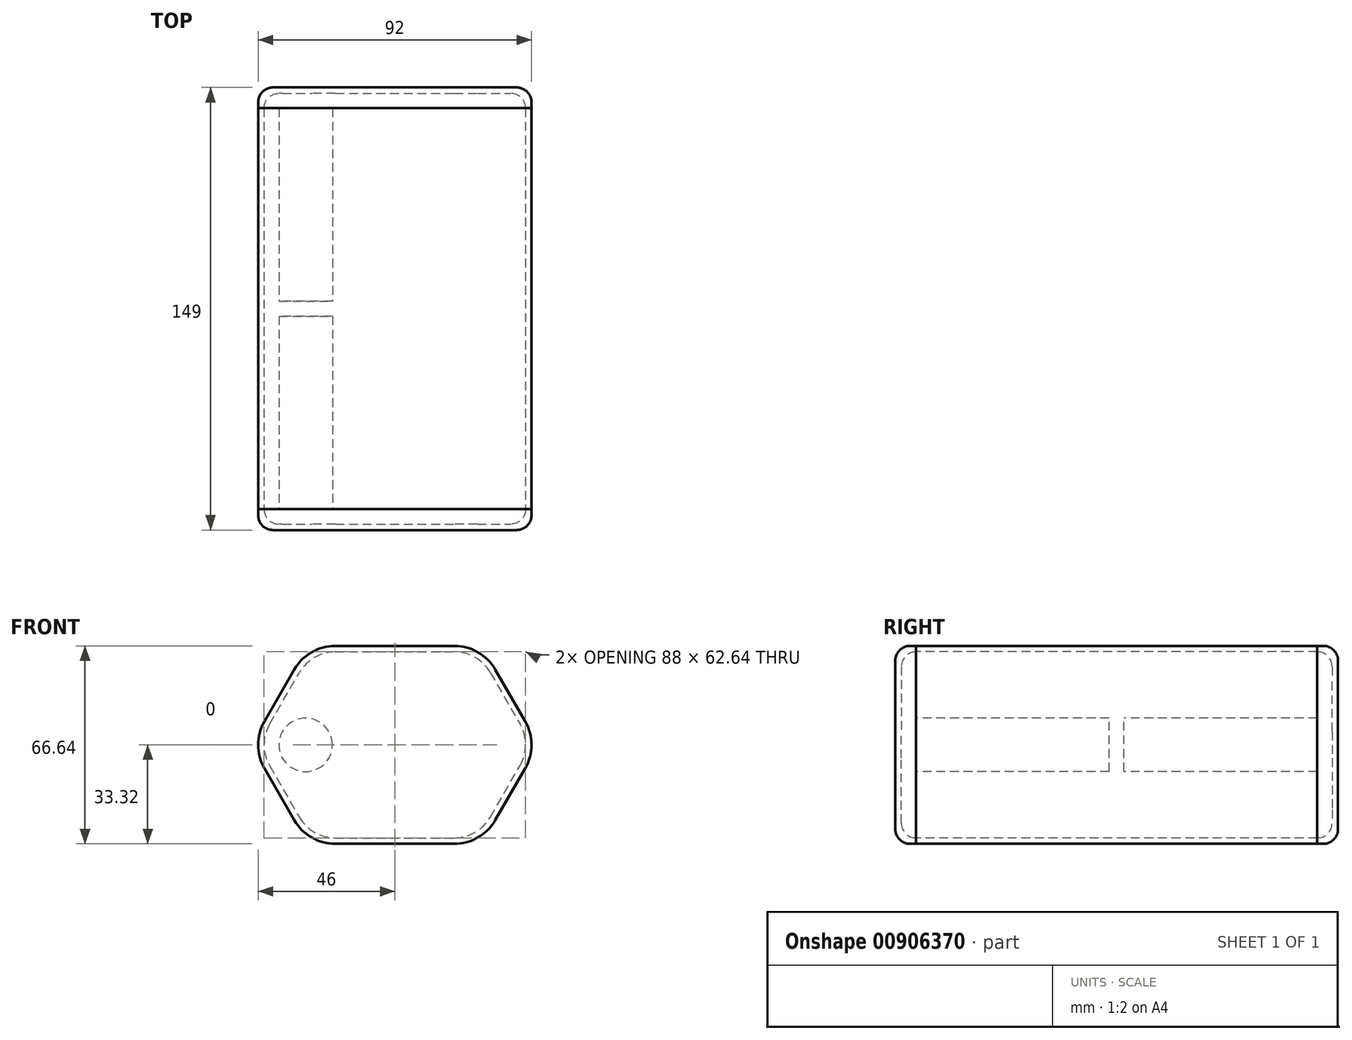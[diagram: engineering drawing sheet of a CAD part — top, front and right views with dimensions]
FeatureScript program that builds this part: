
annotation { "Feature Type Name" : "Feature", "Feature Type Description" : "" }
export const myFeature = defineFeature(function(context is Context, id is Id, definition is map)
    precondition{}
    {
        {
            var Q0;
            Q0=qCreatedBy(makeId("Front.planeOp"),FACE);
            var sketch = newSketch(context, id + "F0", { "sketchPlane" : qUnion([Q0])});
            skCircle(sketch, "E0", {"center": v(0, 0) * mm, "radius": 9 * mm});
            skCircle(sketch, "E1", {"center": v(10, 17.32) * mm, "radius": 9 * mm});
            skCircle(sketch, "E2.1.0.0", {"center": v(20, 0) * mm, "radius": 9 * mm});
            skCircle(sketch, "E2.2.0.0", {"center": v(40, 0) * mm, "radius": 9 * mm});
            skCircle(sketch, "E2.3.0.0", {"center": v(60, 0) * mm, "radius": 9 * mm});
            skLineSegment(sketch, "E2.direction1", {"start": v(0, 0) * mm, "end": v(20, 0) * mm, "construction": true});
            skCircle(sketch, "E3.1.0.0", {"center": v(30, 17.32) * mm, "radius": 9 * mm});
            skCircle(sketch, "E3.2.0.0", {"center": v(50, 17.32) * mm, "radius": 9 * mm});
            skLineSegment(sketch, "E3.direction1", {"start": v(10, 17.32) * mm, "end": v(30, 17.32) * mm, "construction": true});
            skCircle(sketch, "E4", {"center": v(10, -17.32) * mm, "radius": 9 * mm});
            skCircle(sketch, "E5.1.0.0", {"center": v(30, -17.32) * mm, "radius": 9 * mm});
            skCircle(sketch, "E5.2.0.0", {"center": v(50, -17.32) * mm, "radius": 9 * mm});
            skLineSegment(sketch, "E5.direction1", {"start": v(10, -17.32) * mm, "end": v(30, -17.32) * mm, "construction": true});
            skSolve(sketch);
        }
        {
            var Q0;
            Q0=qCreatedBy(makeId("Front.planeOp"),FACE);
            var sketch = newSketch(context, id + "F1", { "sketchPlane" : qUnion([Q0])});
            skArc(sketch, "E6.0", {"start": v(10, 26.32) * mm, "mid": v(5.5, 25.11) * mm, "end": v(2.2, 21.82) * mm});
            skArc(sketch, "E7.0", {"start": v(-7.8, 4.5) * mm, "mid": v(-9, 0) * mm, "end": v(-7.8, -4.5) * mm});
            skArc(sketch, "E8.0", {"start": v(2.2, -21.82) * mm, "mid": v(5.5, -25.11) * mm, "end": v(10, -26.32) * mm});
            skArc(sketch, "E9.0", {"start": v(57.8, 21.82) * mm, "mid": v(54.5, 25.11) * mm, "end": v(50, 26.32) * mm});
            skArc(sketch, "E10.0", {"start": v(67.8, -4.5) * mm, "mid": v(69, 0) * mm, "end": v(67.8, 4.5) * mm});
            skArc(sketch, "E11.0", {"start": v(50, -26.32) * mm, "mid": v(54.5, -25.11) * mm, "end": v(57.8, -21.82) * mm});
            skLineSegment(sketch, "E12", {"start": v(10, 26.32) * mm, "end": v(50, 26.32) * mm});
            skLineSegment(sketch, "E13", {"start": v(57.8, 21.82) * mm, "end": v(67.8, 4.5) * mm});
            skLineSegment(sketch, "E14", {"start": v(57.8, -21.82) * mm, "end": v(67.8, -4.5) * mm});
            skLineSegment(sketch, "E15", {"start": v(10, -26.32) * mm, "end": v(50, -26.32) * mm});
            skLineSegment(sketch, "E16", {"start": v(-7.8, -4.5) * mm, "end": v(2.2, -21.82) * mm});
            skLineSegment(sketch, "E17", {"start": v(-7.8, 4.5) * mm, "end": v(2.2, 21.82) * mm});
            skLineSegment(sketch, "E18.0", {"start": v(10, 31.32) * mm, "end": v(50, 31.32) * mm});
            skArc(sketch, "E18.1", {"start": v(-2.12, -24.32) * mm, "mid": v(3, -29.44) * mm, "end": v(10, -31.32) * mm});
            skLineSegment(sketch, "E18.2", {"start": v(-12.12, -7) * mm, "end": v(-2.12, -24.32) * mm});
            skArc(sketch, "E18.3", {"start": v(-12.12, 7) * mm, "mid": v(-14, 0) * mm, "end": v(-12.12, -7) * mm});
            skLineSegment(sketch, "E18.4", {"start": v(-12.12, 7) * mm, "end": v(-2.12, 24.32) * mm});
            skLineSegment(sketch, "E18.5", {"start": v(10, -31.32) * mm, "end": v(50, -31.32) * mm});
            skArc(sketch, "E18.6", {"start": v(10, 31.32) * mm, "mid": v(3, 29.44) * mm, "end": v(-2.12, 24.32) * mm});
            skArc(sketch, "E18.7", {"start": v(50, -31.32) * mm, "mid": v(57, -29.44) * mm, "end": v(62.12, -24.32) * mm});
            skLineSegment(sketch, "E18.8", {"start": v(62.12, -24.32) * mm, "end": v(72.12, -7) * mm});
            skArc(sketch, "E18.9", {"start": v(72.12, -7) * mm, "mid": v(74, 0) * mm, "end": v(72.12, 7) * mm});
            skLineSegment(sketch, "E18.10", {"start": v(62.12, 24.32) * mm, "end": v(72.12, 7) * mm});
            skArc(sketch, "E18.11", {"start": v(62.12, 24.32) * mm, "mid": v(57, 29.44) * mm, "end": v(50, 31.32) * mm});
            skLineSegment(sketch, "E19.0", {"start": v(10, 33.32) * mm, "end": v(50, 33.32) * mm});
            skArc(sketch, "E19.1", {"start": v(-3.86, -25.32) * mm, "mid": v(2, -31.18) * mm, "end": v(10, -33.32) * mm});
            skLineSegment(sketch, "E19.2", {"start": v(-13.86, -8) * mm, "end": v(-3.86, -25.32) * mm});
            skArc(sketch, "E19.3", {"start": v(-13.86, 8) * mm, "mid": v(-16, 0) * mm, "end": v(-13.86, -8) * mm});
            skLineSegment(sketch, "E19.4", {"start": v(-13.86, 8) * mm, "end": v(-3.86, 25.32) * mm});
            skLineSegment(sketch, "E19.5", {"start": v(10, -33.32) * mm, "end": v(50, -33.32) * mm});
            skArc(sketch, "E19.6", {"start": v(10, 33.32) * mm, "mid": v(2, 31.18) * mm, "end": v(-3.86, 25.32) * mm});
            skArc(sketch, "E19.7", {"start": v(50, -33.32) * mm, "mid": v(58, -31.18) * mm, "end": v(63.86, -25.32) * mm});
            skLineSegment(sketch, "E19.8", {"start": v(63.86, -25.32) * mm, "end": v(73.86, -8) * mm});
            skArc(sketch, "E19.9", {"start": v(73.86, -8) * mm, "mid": v(76, 0) * mm, "end": v(73.86, 8) * mm});
            skLineSegment(sketch, "E19.10", {"start": v(63.86, 25.32) * mm, "end": v(73.86, 8) * mm});
            skArc(sketch, "E19.11", {"start": v(63.86, 25.32) * mm, "mid": v(58, 31.18) * mm, "end": v(50, 33.32) * mm});
            skSolve(sketch);
        }
        {
            var Q0;
            Q0=qCreatedBy(makeId("Front.planeOp"),FACE);
            cPlane(context, id + "F2", {"entities" : qUnion([Q0]), "cplaneType" : CPlaneType.OFFSET, "offset" : 70 * mm, "oppositeDirection" : true, "width" : 150 * mm, "height" : 150 * mm});
        }
        {
            var Q0;
            Q0=qCreatedBy(id+"F2.planeOp",FACE);
            var sketch = newSketch(context, id + "F3", { "sketchPlane" : qUnion([Q0])});
            skCircle(sketch, "E20.0", {"center": v(10, 17.32) * mm, "radius": 9 * mm});
            skCircle(sketch, "E21.0", {"center": v(30, 17.32) * mm, "radius": 9 * mm});
            skCircle(sketch, "E22.0", {"center": v(50, 17.32) * mm, "radius": 9 * mm});
            skCircle(sketch, "E23.0", {"center": v(20, 0) * mm, "radius": 9 * mm});
            skCircle(sketch, "E24.0", {"center": v(0, 0) * mm, "radius": 9 * mm});
            skCircle(sketch, "E25.0", {"center": v(40, 0) * mm, "radius": 9 * mm});
            skCircle(sketch, "E26.0", {"center": v(60, 0) * mm, "radius": 9 * mm});
            skCircle(sketch, "E27.0", {"center": v(30, -17.32) * mm, "radius": 9 * mm});
            skCircle(sketch, "E28.0", {"center": v(10, -17.32) * mm, "radius": 9 * mm});
            skCircle(sketch, "E29.0", {"center": v(50, -17.32) * mm, "radius": 9 * mm});
            skSolve(sketch);
        }
        {
            var Q0;
            Q0=makeQuery(id+"F0.imprint","IMPRINT",FACE,{"disambiguationData":[TD([[makeQuery(id+"F0.imprint","IMPRINT",EDGE,{"derivedFrom":sQuery(id+"F0.wireOp",EDGE,"E0")}),1.0]])]});
            extrude(context, id + "F4", {"entities" : qUnion([Q0]), "oppositeDirection" : true, "depth" : 65 * mm, "offsetDistance" : 25 * mm});
        }
        {
            var Q0;
            Q0=makeQuery(id+"F3.imprint","IMPRINT",FACE,{"disambiguationData":[TD([[makeQuery(id+"F3.imprint","IMPRINT",EDGE,{"derivedFrom":sQuery(id+"F3.wireOp",EDGE,"E24.0")}),1.0]])]});
            extrude(context, id + "F5", {"entities" : qUnion([Q0]), "oppositeDirection" : true, "depth" : 65 * mm, "offsetDistance" : 25 * mm});
        }
        {
            var Q0;
            Q0=makeQuery(id+"F1.imprint","IMPRINT",FACE,{"disambiguationData":[TD([[makeQuery(id+"F1.imprint","IMPRINT",EDGE,{"derivedFrom":sQuery(id+"F1.wireOp",EDGE,"E18.0")}),1.0]])]});
            extrude(context, id + "F6", {"entities" : qUnion([Q0]), "oppositeDirection" : true, "depth" : 135 * mm, "offsetDistance" : 25 * mm});
        }
        {
            var Q0;
            Q0=makeQuery(id+"F6.opExtrude","CAP_FACE",FACE,{"disambiguationData":[OSD([sQuery(id+"F1.wireOp",EDGE,"E18.0"),sQuery(id+"F1.wireOp",EDGE,"E18.1"),sQuery(id+"F1.wireOp",EDGE,"E18.2"),sQuery(id+"F1.wireOp",EDGE,"E18.3"),sQuery(id+"F1.wireOp",EDGE,"E18.4"),sQuery(id+"F1.wireOp",EDGE,"E18.5"),sQuery(id+"F1.wireOp",EDGE,"E18.6"),sQuery(id+"F1.wireOp",EDGE,"E18.7"),sQuery(id+"F1.wireOp",EDGE,"E18.8"),sQuery(id+"F1.wireOp",EDGE,"E18.9"),sQuery(id+"F1.wireOp",EDGE,"E18.10"),sQuery(id+"F1.wireOp",EDGE,"E18.11"),sQuery(id+"F1.wireOp",EDGE,"E19.0"),sQuery(id+"F1.wireOp",EDGE,"E19.1"),sQuery(id+"F1.wireOp",EDGE,"E19.2"),sQuery(id+"F1.wireOp",EDGE,"E19.3"),sQuery(id+"F1.wireOp",EDGE,"E19.4"),sQuery(id+"F1.wireOp",EDGE,"E19.5"),sQuery(id+"F1.wireOp",EDGE,"E19.6"),sQuery(id+"F1.wireOp",EDGE,"E19.7"),sQuery(id+"F1.wireOp",EDGE,"E19.8"),sQuery(id+"F1.wireOp",EDGE,"E19.9"),sQuery(id+"F1.wireOp",EDGE,"E19.10"),sQuery(id+"F1.wireOp",EDGE,"E19.11")])],"isStart":true});
            var sketch = newSketch(context, id + "F7", { "sketchPlane" : qUnion([Q0])});
            skLineSegment(sketch, "E30.0.0", {"start": v(10, -33.32) * mm, "end": v(50, -33.32) * mm});
            skArc(sketch, "E30.0.1", {"start": v(50, -33.32) * mm, "mid": v(58, -31.18) * mm, "end": v(63.86, -25.32) * mm});
            skLineSegment(sketch, "E30.0.2", {"start": v(63.86, -25.32) * mm, "end": v(73.86, -8) * mm});
            skArc(sketch, "E30.0.3", {"start": v(73.86, -8) * mm, "mid": v(76, 0) * mm, "end": v(73.86, 8) * mm});
            skLineSegment(sketch, "E30.0.4", {"start": v(73.86, 8) * mm, "end": v(63.86, 25.32) * mm});
            skArc(sketch, "E30.0.5", {"start": v(63.86, 25.32) * mm, "mid": v(58, 31.18) * mm, "end": v(50, 33.32) * mm});
            skLineSegment(sketch, "E30.0.6", {"start": v(50, 33.32) * mm, "end": v(10, 33.32) * mm});
            skArc(sketch, "E30.0.7", {"start": v(10, 33.32) * mm, "mid": v(2, 31.18) * mm, "end": v(-3.86, 25.32) * mm});
            skLineSegment(sketch, "E30.0.8", {"start": v(-3.86, 25.32) * mm, "end": v(-13.86, 8) * mm});
            skArc(sketch, "E30.0.9", {"start": v(-13.86, 8) * mm, "mid": v(-16, 0) * mm, "end": v(-13.86, -8) * mm});
            skLineSegment(sketch, "E30.0.10", {"start": v(-13.86, -8) * mm, "end": v(-3.86, -25.32) * mm});
            skArc(sketch, "E30.0.11", {"start": v(-3.86, -25.32) * mm, "mid": v(2, -31.18) * mm, "end": v(10, -33.32) * mm});
            skArc(sketch, "E31.0", {"start": v(10, 31.32) * mm, "mid": v(3, 29.44) * mm, "end": v(-2.12, 24.32) * mm});
            skLineSegment(sketch, "E32.0", {"start": v(10, 31.32) * mm, "end": v(50, 31.32) * mm});
            skArc(sketch, "E33.0", {"start": v(62.12, 24.32) * mm, "mid": v(57, 29.44) * mm, "end": v(50, 31.32) * mm});
            skLineSegment(sketch, "E34.0", {"start": v(62.12, 24.32) * mm, "end": v(72.12, 7) * mm});
            skArc(sketch, "E35.0", {"start": v(-12.12, 7) * mm, "mid": v(-14, 0) * mm, "end": v(-12.12, -7) * mm});
            skLineSegment(sketch, "E36.0", {"start": v(-12.12, 7) * mm, "end": v(-2.12, 24.32) * mm});
            skLineSegment(sketch, "E37.0", {"start": v(-12.12, -7) * mm, "end": v(-2.12, -24.32) * mm});
            skArc(sketch, "E38.0", {"start": v(-2.12, -24.32) * mm, "mid": v(3, -29.44) * mm, "end": v(10, -31.32) * mm});
            skLineSegment(sketch, "E39.0", {"start": v(10, -31.32) * mm, "end": v(50, -31.32) * mm});
            skArc(sketch, "E40.0", {"start": v(50, -31.32) * mm, "mid": v(57, -29.44) * mm, "end": v(62.12, -24.32) * mm});
            skLineSegment(sketch, "E41.0", {"start": v(62.12, -24.32) * mm, "end": v(72.12, -7) * mm});
            skArc(sketch, "E42.0", {"start": v(72.12, -7) * mm, "mid": v(74, 0) * mm, "end": v(72.12, 7) * mm});
            skSolve(sketch);
        }
        {
            var Q0;
            Q0=makeQuery(id+"F7.imprint","IMPRINT",FACE,{"disambiguationData":[TD([[makeQuery(id+"F7.imprint","IMPRINT",EDGE,{"derivedFrom":sQuery(id+"F7.wireOp",EDGE,"E30.0.0")}),1.0]])]});
            extrude(context, id + "F8", {"entities" : qUnion([Q0]), "depth" : 5 * mm, "offsetDistance" : 25 * mm});
        }
        {
            var Q0;
            Q0=makeQuery(id+"F8.opExtrude","CAP_FACE",FACE,{"disambiguationData":[OSD([sQuery(id+"F7.wireOp",EDGE,"E30.0.0"),sQuery(id+"F7.wireOp",EDGE,"E30.0.1"),sQuery(id+"F7.wireOp",EDGE,"E30.0.2"),sQuery(id+"F7.wireOp",EDGE,"E30.0.3"),sQuery(id+"F7.wireOp",EDGE,"E30.0.4"),sQuery(id+"F7.wireOp",EDGE,"E30.0.5"),sQuery(id+"F7.wireOp",EDGE,"E30.0.6"),sQuery(id+"F7.wireOp",EDGE,"E30.0.7"),sQuery(id+"F7.wireOp",EDGE,"E30.0.8"),sQuery(id+"F7.wireOp",EDGE,"E30.0.9"),sQuery(id+"F7.wireOp",EDGE,"E30.0.10"),sQuery(id+"F7.wireOp",EDGE,"E30.0.11"),sQuery(id+"F7.wireOp",EDGE,"E31.0"),sQuery(id+"F7.wireOp",EDGE,"E32.0"),sQuery(id+"F7.wireOp",EDGE,"E33.0"),sQuery(id+"F7.wireOp",EDGE,"E34.0"),sQuery(id+"F7.wireOp",EDGE,"E35.0"),sQuery(id+"F7.wireOp",EDGE,"E36.0"),sQuery(id+"F7.wireOp",EDGE,"E37.0"),sQuery(id+"F7.wireOp",EDGE,"E38.0"),sQuery(id+"F7.wireOp",EDGE,"E39.0"),sQuery(id+"F7.wireOp",EDGE,"E40.0"),sQuery(id+"F7.wireOp",EDGE,"E41.0"),sQuery(id+"F7.wireOp",EDGE,"E42.0")])],"isStart":false});
            var sketch = newSketch(context, id + "F9", { "sketchPlane" : qUnion([Q0])});
            skArc(sketch, "E43.0.0", {"start": v(-3.86, -25.32) * mm, "mid": v(2, -31.18) * mm, "end": v(10, -33.32) * mm});
            skLineSegment(sketch, "E43.0.1", {"start": v(10, -33.32) * mm, "end": v(50, -33.32) * mm});
            skArc(sketch, "E43.0.2", {"start": v(50, -33.32) * mm, "mid": v(58, -31.18) * mm, "end": v(63.86, -25.32) * mm});
            skLineSegment(sketch, "E43.0.3", {"start": v(63.86, -25.32) * mm, "end": v(73.86, -8) * mm});
            skArc(sketch, "E43.0.4", {"start": v(73.86, -8) * mm, "mid": v(76, 0) * mm, "end": v(73.86, 8) * mm});
            skLineSegment(sketch, "E43.0.5", {"start": v(73.86, 8) * mm, "end": v(63.86, 25.32) * mm});
            skArc(sketch, "E43.0.6", {"start": v(63.86, 25.32) * mm, "mid": v(58, 31.18) * mm, "end": v(50, 33.32) * mm});
            skLineSegment(sketch, "E43.0.7", {"start": v(50, 33.32) * mm, "end": v(10, 33.32) * mm});
            skArc(sketch, "E43.0.8", {"start": v(10, 33.32) * mm, "mid": v(2, 31.18) * mm, "end": v(-3.86, 25.32) * mm});
            skLineSegment(sketch, "E43.0.9", {"start": v(-3.86, 25.32) * mm, "end": v(-13.86, 8) * mm});
            skArc(sketch, "E43.0.10", {"start": v(-13.86, 8) * mm, "mid": v(-16, 0) * mm, "end": v(-13.86, -8) * mm});
            skLineSegment(sketch, "E43.0.11", {"start": v(-13.86, -8) * mm, "end": v(-3.86, -25.32) * mm});
            skSolve(sketch);
        }
        {
            var Q0;
            Q0=makeQuery(id+"F9.imprint","IMPRINT",FACE,{"disambiguationData":[TD([[makeQuery(id+"F9.imprint","IMPRINT",EDGE,{"derivedFrom":sQuery(id+"F9.wireOp",EDGE,"E43.0.0")}),1.0]])]});
            var Q1;
            Q1=makeQuery(id+"F9.imprint","IMPRINT",FACE,{"disambiguationData":[TD([[makeQuery(id+"F9.imprint","IMPRINT",EDGE,{"derivedFrom":makeQuery(id+"F8.opExtrude","CAP_EDGE",EDGE,{"disambiguationData":[OSD([sQuery(id+"F7.wireOp",EDGE,"E31.0")])],"isStart":false})}),1.0]])]});
            extrude(context, id + "F10", {"entities" : qUnion([Q0, Q1]), "operationType" : NewBodyOperationType.ADD, "depth" : 2 * mm, "offsetDistance" : 25 * mm});
        }
        {
            var Q0;
            Q0=makeQuery(id+"F10.opExtrude","CAP_FACE",FACE,{"disambiguationData":[OSD([sQuery(id+"F9.wireOp",EDGE,"E43.0.0"),sQuery(id+"F9.wireOp",EDGE,"E43.0.1"),sQuery(id+"F9.wireOp",EDGE,"E43.0.2"),sQuery(id+"F9.wireOp",EDGE,"E43.0.3"),sQuery(id+"F9.wireOp",EDGE,"E43.0.4"),sQuery(id+"F9.wireOp",EDGE,"E43.0.5"),sQuery(id+"F9.wireOp",EDGE,"E43.0.6"),sQuery(id+"F9.wireOp",EDGE,"E43.0.7"),sQuery(id+"F9.wireOp",EDGE,"E43.0.8"),sQuery(id+"F9.wireOp",EDGE,"E43.0.9"),sQuery(id+"F9.wireOp",EDGE,"E43.0.10"),sQuery(id+"F9.wireOp",EDGE,"E43.0.11")])],"isStart":false});
            fillet(context, id + "F11", {"entities" : qUnion([Q0]), "radius" : 5 * mm, "tangentPropagation" : true, "allowEdgeOverflow" : false});
        }
        {
            var Q0;
            Q0=makeQuery(id+"F10.opExtrude","CAP_FACE",FACE,{"disambiguationData":[OSD([sQuery(id+"F9.wireOp",EDGE,"E43.0.0"),sQuery(id+"F9.wireOp",EDGE,"E43.0.1"),sQuery(id+"F9.wireOp",EDGE,"E43.0.2"),sQuery(id+"F9.wireOp",EDGE,"E43.0.3"),sQuery(id+"F9.wireOp",EDGE,"E43.0.4"),sQuery(id+"F9.wireOp",EDGE,"E43.0.5"),sQuery(id+"F9.wireOp",EDGE,"E43.0.6"),sQuery(id+"F9.wireOp",EDGE,"E43.0.7"),sQuery(id+"F9.wireOp",EDGE,"E43.0.8"),sQuery(id+"F9.wireOp",EDGE,"E43.0.9"),sQuery(id+"F9.wireOp",EDGE,"E43.0.10"),sQuery(id+"F9.wireOp",EDGE,"E43.0.11")])],"isStart":true});
            fillet(context, id + "F12", {"entities" : qUnion([Q0]), "radius" : 5 * mm, "tangentPropagation" : true, "allowEdgeOverflow" : false});
        }
        {
            var Q0;
            Q0=qCreatedBy(makeId("Front.planeOp"),FACE);
            cPlane(context, id + "F13", {"entities" : qUnion([Q0]), "cplaneType" : CPlaneType.OFFSET, "offset" : 67.5 * mm, "oppositeDirection" : true, "width" : 150 * mm, "height" : 150 * mm});
        }
        {
            var Q0;
            Q0=makeQuery(id+"F8.opExtrude","SWEPT_BODY",BODY,{"disambiguationData":[OSD([sQuery(id+"F7.wireOp",EDGE,"E30.0.0"),sQuery(id+"F7.wireOp",EDGE,"E30.0.1"),sQuery(id+"F7.wireOp",EDGE,"E30.0.2"),sQuery(id+"F7.wireOp",EDGE,"E30.0.3"),sQuery(id+"F7.wireOp",EDGE,"E30.0.4"),sQuery(id+"F7.wireOp",EDGE,"E30.0.5"),sQuery(id+"F7.wireOp",EDGE,"E30.0.6"),sQuery(id+"F7.wireOp",EDGE,"E30.0.7"),sQuery(id+"F7.wireOp",EDGE,"E30.0.8"),sQuery(id+"F7.wireOp",EDGE,"E30.0.9"),sQuery(id+"F7.wireOp",EDGE,"E30.0.10"),sQuery(id+"F7.wireOp",EDGE,"E30.0.11"),sQuery(id+"F7.wireOp",EDGE,"E31.0"),sQuery(id+"F7.wireOp",EDGE,"E32.0"),sQuery(id+"F7.wireOp",EDGE,"E33.0"),sQuery(id+"F7.wireOp",EDGE,"E34.0"),sQuery(id+"F7.wireOp",EDGE,"E35.0"),sQuery(id+"F7.wireOp",EDGE,"E36.0"),sQuery(id+"F7.wireOp",EDGE,"E37.0"),sQuery(id+"F7.wireOp",EDGE,"E38.0"),sQuery(id+"F7.wireOp",EDGE,"E39.0"),sQuery(id+"F7.wireOp",EDGE,"E40.0"),sQuery(id+"F7.wireOp",EDGE,"E41.0"),sQuery(id+"F7.wireOp",EDGE,"E42.0")])]});
            var Q1;
            Q1=qCreatedBy(id+"F13.planeOp",FACE);
            mirror(context, id + "F14", {"entities" : qUnion([Q0]), "mirrorPlane" : qUnion([Q1])});
        }
    });
